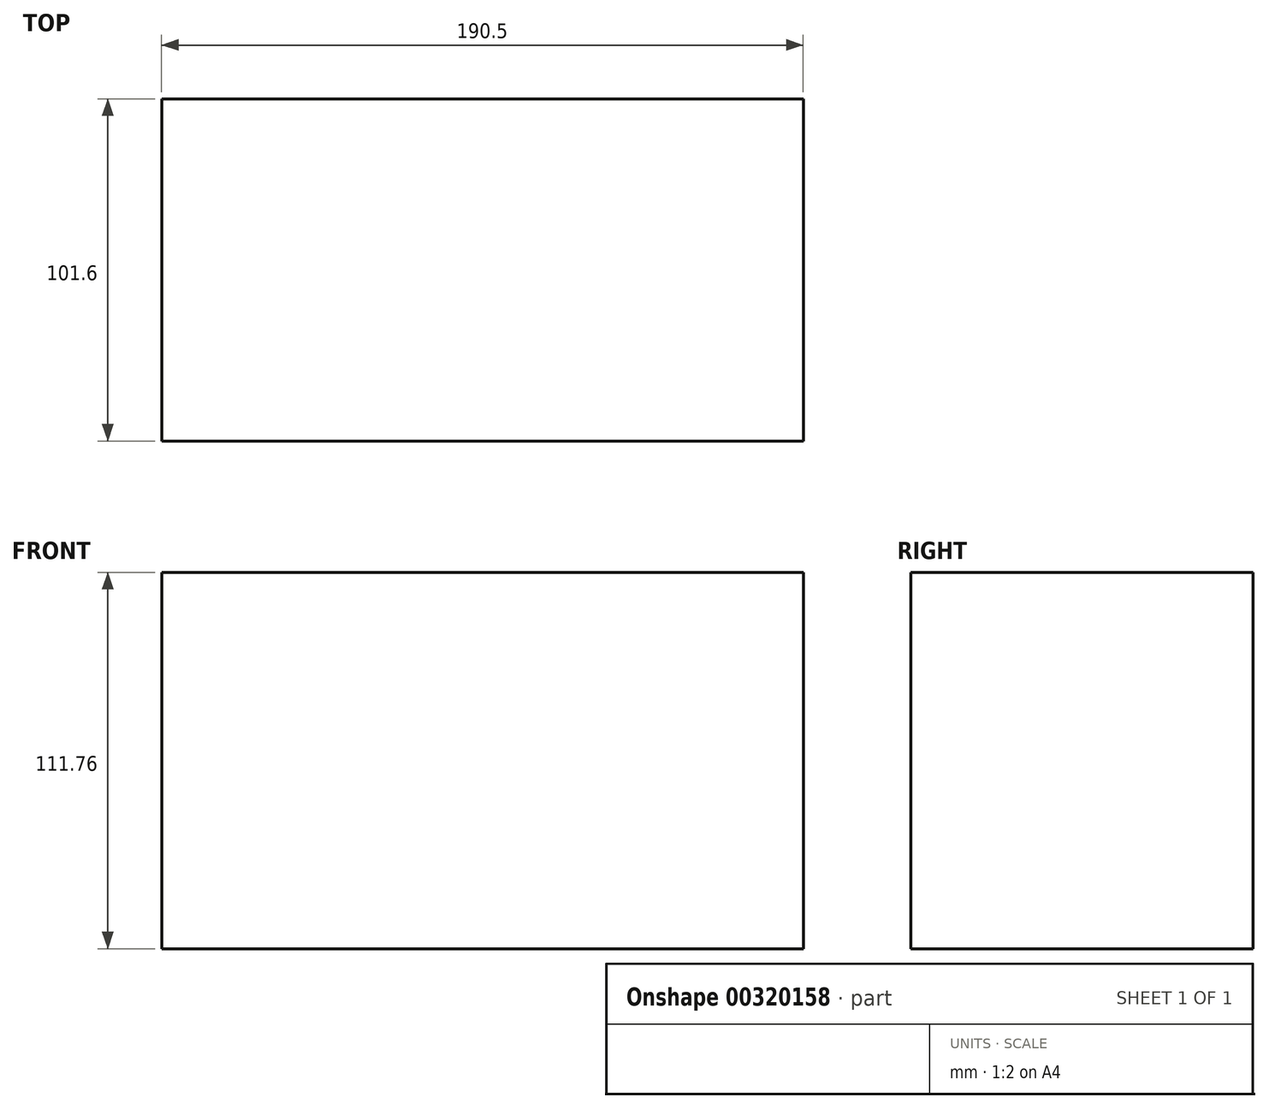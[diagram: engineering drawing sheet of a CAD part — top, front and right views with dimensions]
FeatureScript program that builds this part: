
annotation { "Feature Type Name" : "Feature", "Feature Type Description" : "" }
export const myFeature = defineFeature(function(context is Context, id is Id, definition is map)
    precondition{}
    {
        {
            var Q0;
            Q0=qCreatedBy(makeId("Front.planeOp"),FACE);
            var sketch = newSketch(context, id + "F0", { "sketchPlane" : qUnion([Q0])});
            skLineSegment(sketch, "E0.bottom", {"start": v(-89.9, 29.53) * mm, "end": v(100.6, 29.53) * mm});
            skLineSegment(sketch, "E0.top", {"start": v(-89.9, -82.23) * mm, "end": v(100.6, -82.23) * mm});
            skLineSegment(sketch, "E0.left", {"start": v(-89.9, 29.53) * mm, "end": v(-89.9, -82.23) * mm});
            skLineSegment(sketch, "E0.right", {"start": v(100.6, 29.53) * mm, "end": v(100.6, -82.23) * mm});
            skSolve(sketch);
        }
        {
            var Q0;
            Q0=makeQuery(id+"F0.imprint","IMPRINT",FACE,{"disambiguationData":[TD([[makeQuery(id+"F0.imprint","IMPRINT",EDGE,{"derivedFrom":sQuery(id+"F0.wireOp",EDGE,"E0.bottom")}),-1.0]])]});
            extrude(context, id + "F1", {"entities" : qUnion([Q0]), "offsetDistance" : 25.4 * mm, "depth" : 101.6 * mm});
        }
    });
